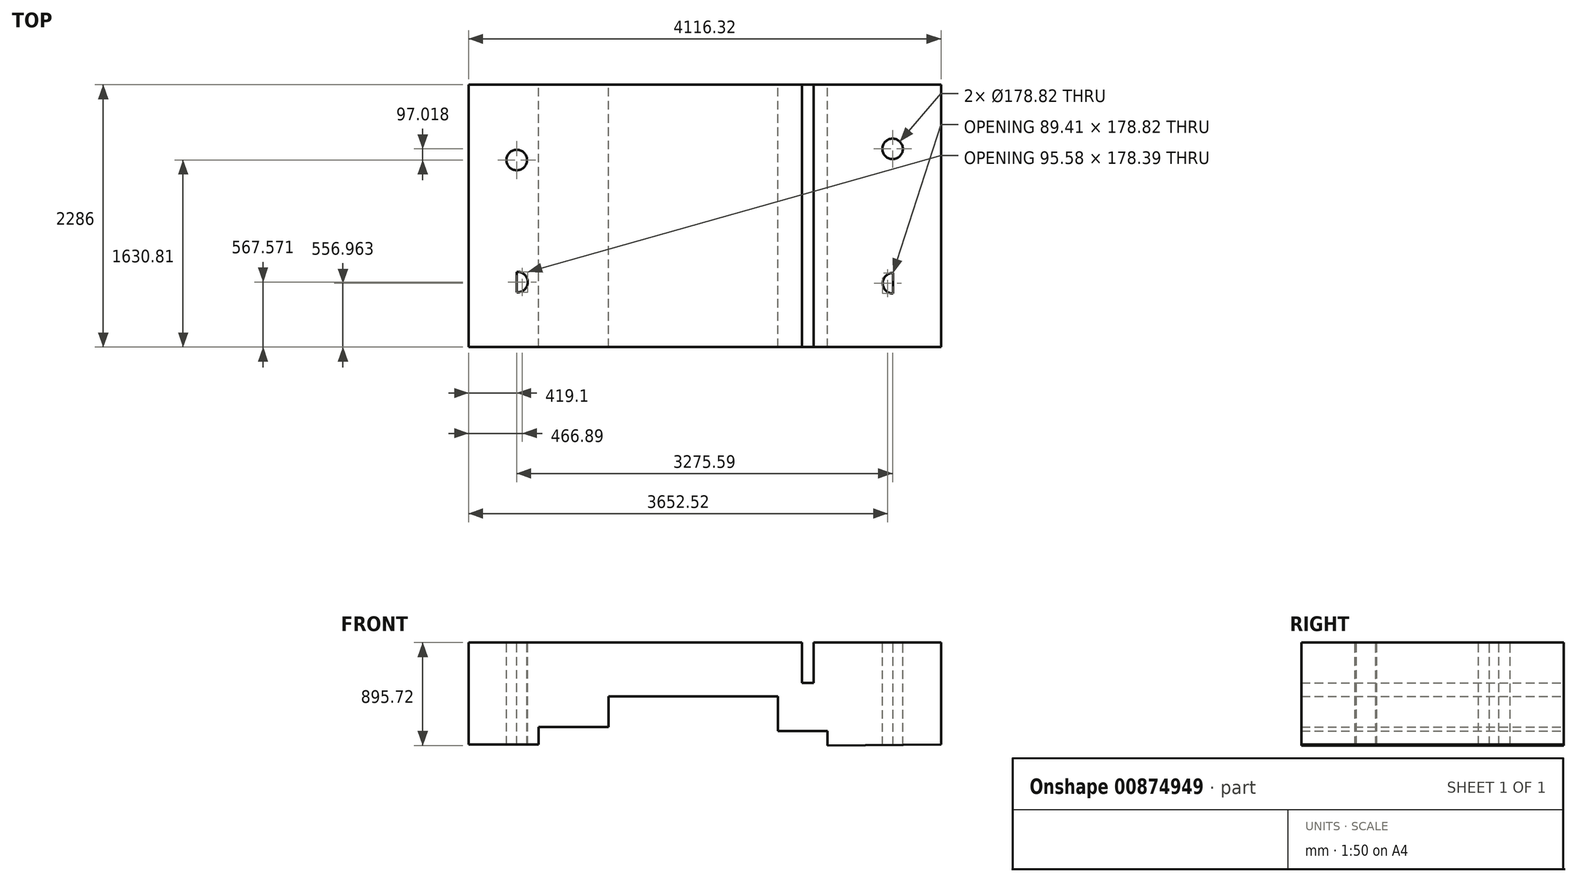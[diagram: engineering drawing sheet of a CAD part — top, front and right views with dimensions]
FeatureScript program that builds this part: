
annotation { "Feature Type Name" : "Feature", "Feature Type Description" : "" }
export const myFeature = defineFeature(function(context is Context, id is Id, definition is map)
    precondition{}
    {
        {
            var Q0;
            Q0=qCreatedBy(makeId("Front.planeOp"),FACE);
            var sketch = newSketch(context, id + "F0", { "sketchPlane" : qUnion([Q0])});
            skLineSegment(sketch, "E0", {"start": v(-1563.65, -413.16) * mm, "end": v(-1563.65, -259.16) * mm});
            skLineSegment(sketch, "E1", {"start": v(-1563.65, -259.16) * mm, "end": v(-954.81, -259.16) * mm});
            skLineSegment(sketch, "E2", {"start": v(-954.81, -259.16) * mm, "end": v(-954.81, 6.84) * mm});
            skLineSegment(sketch, "E3", {"start": v(-954.81, 6.84) * mm, "end": v(522.7, 6.84) * mm});
            skLineSegment(sketch, "E4", {"start": v(522.7, 6.84) * mm, "end": v(522.7, -294.15) * mm});
            skLineSegment(sketch, "E5", {"start": v(522.7, -294.15) * mm, "end": v(952.47, -294.15) * mm});
            skLineSegment(sketch, "E6", {"start": v(952.47, -294.15) * mm, "end": v(952.47, -419.88) * mm});
            skLineSegment(sketch, "E7", {"start": v(1396.75, -413.16) * mm, "end": v(1396.75, -419.88) * mm});
            skLineSegment(sketch, "E8", {"start": v(1943.07, -413.16) * mm, "end": v(1943.07, 475.84) * mm});
            skLineSegment(sketch, "E9", {"start": v(1943.07, 475.84) * mm, "end": v(832.33, 475.84) * mm});
            skLineSegment(sketch, "E10", {"start": v(832.33, 475.84) * mm, "end": v(832.33, 125.84) * mm});
            skLineSegment(sketch, "E11", {"start": v(832.33, 125.84) * mm, "end": v(731.5, 125.84) * mm});
            skLineSegment(sketch, "E12", {"start": v(731.5, 125.84) * mm, "end": v(731.5, 475.84) * mm});
            skLineSegment(sketch, "E13", {"start": v(731.5, 475.84) * mm, "end": v(-2173.25, 475.84) * mm});
            skLineSegment(sketch, "E14", {"start": v(-2173.25, -413.16) * mm, "end": v(-1563.65, -413.16) * mm});
            skLineSegment(sketch, "E15", {"start": v(-2173.25, -413.16) * mm, "end": v(-2173.25, 475.84) * mm});
            skLineSegment(sketch, "E16", {"start": v(952.47, -419.88) * mm, "end": v(1943.07, -413.16) * mm});
            skSolve(sketch);
        }
        {
            var Q0;
            Q0=makeQuery(id+"F0.imprint","IMPRINT",FACE,{"disambiguationData":[TD([[makeQuery(id+"F0.imprint","IMPRINT",EDGE,{"derivedFrom":sQuery(id+"F0.wireOp",EDGE,"E0")}),1.0]])]});
            extrude(context, id + "F1", {"entities" : qUnion([Q0]), "depth" : 2286 * mm, "offsetDistance" : 25.4 * mm});
        }
        {
            var Q0;
            Q0=makeQuery(id+"F1.opExtrude","SWEPT_FACE",FACE,{"disambiguationData":[OSD([sQuery(id+"F0.wireOp",EDGE,"E13")])]});
            var sketch = newSketch(context, id + "F2", { "sketchPlane" : qUnion([Q0])});
            skCircle(sketch, "E17", {"center": v(1521.44, -558.17) * mm, "radius": 89.4 * mm});
            skCircle(sketch, "E18", {"center": v(1523.97, -1729.04) * mm, "radius": 89.4 * mm});
            skCircle(sketch, "E19", {"center": v(-1754.15, -655.2) * mm, "radius": 89.4 * mm});
            skCircle(sketch, "E20", {"center": v(-1747.98, -1718.43) * mm, "radius": 89.4 * mm});
            skLineSegment(sketch, "E21", {"start": v(-2070.96, -1727.2) * mm, "end": v(1766.52, -1727.2) * mm});
            skLineSegment(sketch, "E22", {"start": v(-2292.53, -558.8) * mm, "end": v(2187.3, -558.8) * mm});
            skLineSegment(sketch, "E23", {"start": v(-1754.15, 177.76) * mm, "end": v(-1754.15, -2601.37) * mm});
            skLineSegment(sketch, "E24", {"start": v(1523.97, 325.09) * mm, "end": v(1523.97, -2706.7) * mm});
            skSolve(sketch);
        }
        {
            var Q0;
            {var subQ0=sQuery(id+"F2.wireOp",EDGE,"E23");var subQ1=sQuery(id+"F2.wireOp",EDGE,"E19");var subQ2=makeQuery(id+"F2.imprint","INTERSECT",VERTEX,{"disambiguationData":[OD(0.0)],"derivedFrom":[subQ1,subQ0]});Q0=makeQuery(id+"F2.imprint","IMPRINT",FACE,{"disambiguationData":[TD([[makeQuery(id+"F2.imprint","IMPRINT",EDGE,{"disambiguationData":[TD([[subQ2,-1.0]])],"derivedFrom":subQ1}),1.0]])]});}
            var Q1;
            {var subQ0=sQuery(id+"F2.wireOp",EDGE,"E21");var subQ1=sQuery(id+"F2.wireOp",EDGE,"E20");var subQ2=makeQuery(id+"F2.imprint","INTERSECT",VERTEX,{"disambiguationData":[OD(0.0)],"derivedFrom":[subQ1,subQ0]});Q1=makeQuery(id+"F2.imprint","IMPRINT",FACE,{"disambiguationData":[TD([[makeQuery(id+"F2.imprint","IMPRINT",EDGE,{"disambiguationData":[TD([[subQ2,1.0]])],"derivedFrom":subQ1}),1.0]])]});}
            var Q2;
            {var subQ0=sQuery(id+"F2.wireOp",EDGE,"E21");var subQ1=sQuery(id+"F2.wireOp",EDGE,"E20");var subQ2=makeQuery(id+"F2.imprint","INTERSECT",VERTEX,{"disambiguationData":[OD(0.0)],"derivedFrom":[subQ1,subQ0]});Q2=makeQuery(id+"F2.imprint","IMPRINT",FACE,{"disambiguationData":[TD([[makeQuery(id+"F2.imprint","IMPRINT",EDGE,{"disambiguationData":[TD([[subQ2,-1.0]])],"derivedFrom":subQ1}),1.0]])]});}
            var Q3;
            {var subQ0=sQuery(id+"F2.wireOp",EDGE,"E23");var subQ1=sQuery(id+"F2.wireOp",EDGE,"E20");var subQ2=makeQuery(id+"F2.imprint","INTERSECT",VERTEX,{"disambiguationData":[OD(1.0)],"derivedFrom":[subQ1,subQ0]});Q3=makeQuery(id+"F2.imprint","IMPRINT",FACE,{"disambiguationData":[TD([[makeQuery(id+"F2.imprint","IMPRINT",EDGE,{"disambiguationData":[TD([[subQ2,-1.0]])],"derivedFrom":subQ1}),1.0]])]});}
            var Q4;
            {var subQ0=sQuery(id+"F2.wireOp",EDGE,"E23");var subQ1=sQuery(id+"F2.wireOp",EDGE,"E20");var subQ2=makeQuery(id+"F2.imprint","INTERSECT",VERTEX,{"disambiguationData":[OD(0.0)],"derivedFrom":[subQ1,subQ0]});Q4=makeQuery(id+"F2.imprint","IMPRINT",FACE,{"disambiguationData":[TD([[makeQuery(id+"F2.imprint","IMPRINT",EDGE,{"disambiguationData":[TD([[subQ2,1.0]])],"derivedFrom":subQ1}),1.0]])]});}
            var Q5;
            {var subQ0=sQuery(id+"F2.wireOp",EDGE,"E23");var subQ1=sQuery(id+"F2.wireOp",EDGE,"E19");var subQ2=makeQuery(id+"F2.imprint","INTERSECT",VERTEX,{"disambiguationData":[OD(0.0)],"derivedFrom":[subQ1,subQ0]});Q5=makeQuery(id+"F2.imprint","IMPRINT",FACE,{"disambiguationData":[TD([[makeQuery(id+"F2.imprint","IMPRINT",EDGE,{"disambiguationData":[TD([[subQ2,1.0]])],"derivedFrom":subQ1}),1.0]])]});}
            var Q6;
            {var subQ0=sQuery(id+"F2.wireOp",EDGE,"E22");var subQ1=sQuery(id+"F2.wireOp",EDGE,"E17");var subQ2=makeQuery(id+"F2.imprint","INTERSECT",VERTEX,{"disambiguationData":[OD(1.0)],"derivedFrom":[subQ1,subQ0]});Q6=makeQuery(id+"F2.imprint","IMPRINT",FACE,{"disambiguationData":[TD([[makeQuery(id+"F2.imprint","IMPRINT",EDGE,{"disambiguationData":[TD([[subQ2,-1.0]])],"derivedFrom":subQ1}),1.0]])]});}
            var Q7;
            {var subQ0=sQuery(id+"F2.wireOp",EDGE,"E24");var subQ1=sQuery(id+"F2.wireOp",EDGE,"E17");var subQ2=makeQuery(id+"F2.imprint","INTERSECT",VERTEX,{"disambiguationData":[OD(0.0)],"derivedFrom":[subQ1,subQ0]});Q7=makeQuery(id+"F2.imprint","IMPRINT",FACE,{"disambiguationData":[TD([[makeQuery(id+"F2.imprint","IMPRINT",EDGE,{"disambiguationData":[TD([[subQ2,-1.0]])],"derivedFrom":subQ1}),1.0]])]});}
            var Q8;
            {var subQ0=sQuery(id+"F2.wireOp",EDGE,"E24");var subQ1=sQuery(id+"F2.wireOp",EDGE,"E17");var subQ2=makeQuery(id+"F2.imprint","INTERSECT",VERTEX,{"disambiguationData":[OD(0.0)],"derivedFrom":[subQ1,subQ0]});Q8=makeQuery(id+"F2.imprint","IMPRINT",FACE,{"disambiguationData":[TD([[makeQuery(id+"F2.imprint","IMPRINT",EDGE,{"disambiguationData":[TD([[subQ2,1.0]])],"derivedFrom":subQ1}),1.0]])]});}
            var Q9;
            {var subQ0=sQuery(id+"F2.wireOp",EDGE,"E22");var subQ1=sQuery(id+"F2.wireOp",EDGE,"E17");var subQ2=makeQuery(id+"F2.imprint","INTERSECT",VERTEX,{"disambiguationData":[OD(0.0)],"derivedFrom":[subQ1,subQ0]});Q9=makeQuery(id+"F2.imprint","IMPRINT",FACE,{"disambiguationData":[TD([[makeQuery(id+"F2.imprint","IMPRINT",EDGE,{"disambiguationData":[TD([[subQ2,1.0]])],"derivedFrom":subQ1}),1.0]])]});}
            var Q10;
            {var subQ0=sQuery(id+"F2.wireOp",EDGE,"E24");var subQ1=sQuery(id+"F2.wireOp",EDGE,"E18");var subQ2=makeQuery(id+"F2.imprint","INTERSECT",VERTEX,{"disambiguationData":[OD(1.0)],"derivedFrom":[subQ1,subQ0]});Q10=makeQuery(id+"F2.imprint","IMPRINT",FACE,{"disambiguationData":[TD([[makeQuery(id+"F2.imprint","IMPRINT",EDGE,{"disambiguationData":[TD([[subQ2,-1.0]])],"derivedFrom":subQ1}),1.0]])]});}
            var Q11;
            {var subQ0=sQuery(id+"F2.wireOp",EDGE,"E21");var subQ1=sQuery(id+"F2.wireOp",EDGE,"E18");var subQ2=makeQuery(id+"F2.imprint","INTERSECT",VERTEX,{"disambiguationData":[OD(0.0)],"derivedFrom":[subQ1,subQ0]});Q11=makeQuery(id+"F2.imprint","IMPRINT",FACE,{"disambiguationData":[TD([[makeQuery(id+"F2.imprint","IMPRINT",EDGE,{"disambiguationData":[TD([[subQ2,-1.0]])],"derivedFrom":subQ1}),1.0]])]});}
            var Q12;
            {var subQ0=sQuery(id+"F2.wireOp",EDGE,"E21");var subQ1=sQuery(id+"F2.wireOp",EDGE,"E18");var subQ2=makeQuery(id+"F2.imprint","INTERSECT",VERTEX,{"disambiguationData":[OD(0.0)],"derivedFrom":[subQ1,subQ0]});Q12=makeQuery(id+"F2.imprint","IMPRINT",FACE,{"disambiguationData":[TD([[makeQuery(id+"F2.imprint","IMPRINT",EDGE,{"disambiguationData":[TD([[subQ2,1.0]])],"derivedFrom":subQ1}),1.0]])]});}
            var Q13;
            {var subQ0=sQuery(id+"F2.wireOp",EDGE,"E24");var subQ1=sQuery(id+"F2.wireOp",EDGE,"E18");var subQ2=makeQuery(id+"F2.imprint","INTERSECT",VERTEX,{"disambiguationData":[OD(0.0)],"derivedFrom":[subQ1,subQ0]});Q13=makeQuery(id+"F2.imprint","IMPRINT",FACE,{"disambiguationData":[TD([[makeQuery(id+"F2.imprint","IMPRINT",EDGE,{"disambiguationData":[TD([[subQ2,1.0]])],"derivedFrom":subQ1}),1.0]])]});}
            extrude(context, id + "F3", {"entities" : qUnion([Q0, Q1, Q2, Q3, Q4, Q5, Q6, Q7, Q8, Q9, Q10, Q11, Q12, Q13]), "operationType" : NewBodyOperationType.REMOVE, "endBound" : BoundingType.THROUGH_ALL, "oppositeDirection" : true, "depth" : 25.4 * mm, "offsetDistance" : 25.4 * mm});
        }
    });
